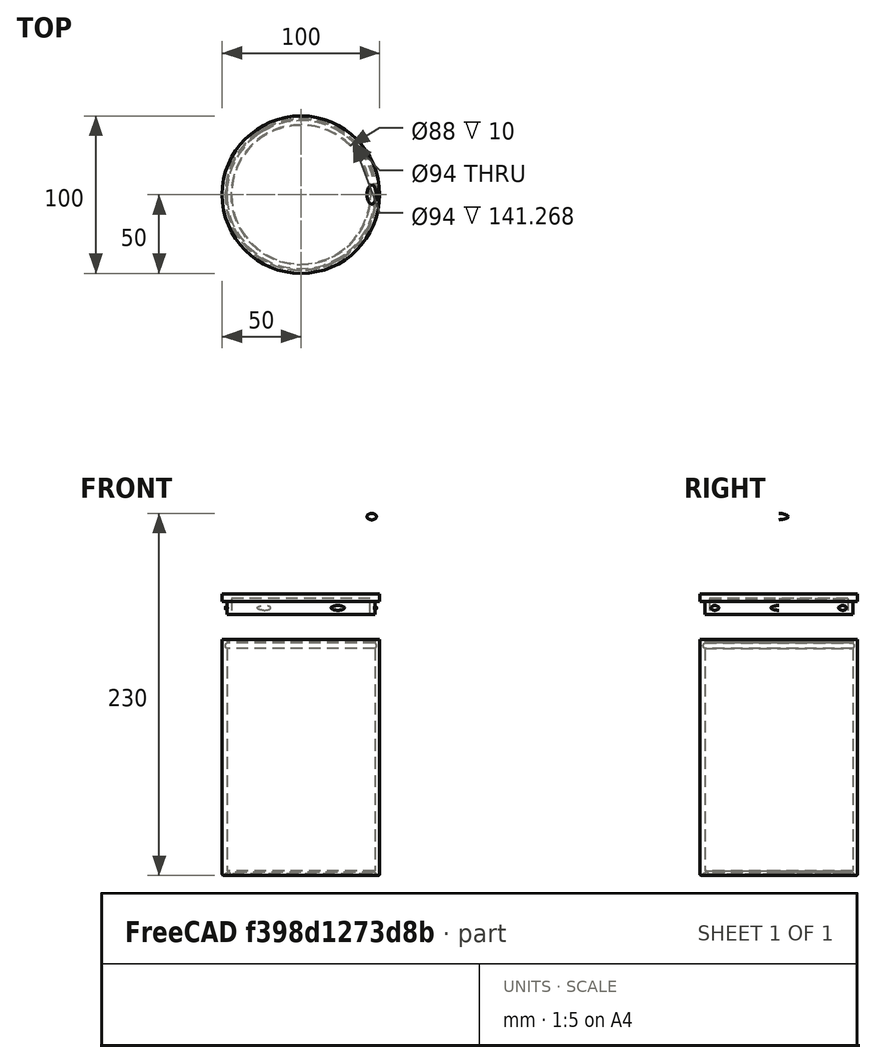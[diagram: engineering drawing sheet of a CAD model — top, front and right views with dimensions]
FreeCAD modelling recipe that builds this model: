
FCSTD DOCUMENT  (FreeCAD 0.20R28811 (Git))
Label: Cub_Escombreries
License: All rights reserved
LicenseURL: http://en.wikipedia.org/wiki/All_rights_reserved
objects: Part::Cylinder×7, Part::Cut×5, Part::Fuse×4, Part::Ellipsoid×2, Part::FeaturePython×2, Part::Torus×2, Part::Thickness×1, Part::Fillet×1, Part::Part2DObjectPython×1, Part::Chamfer×1
note: 24 computed .brp shape members not serialized (recipe doc carries the construction recipe); baked Part::Feature solids carry a one-line shape summary decoded from their .brp

FEATURE [Part::Cylinder] Cylinder
  Angle = 360
  AttacherType = Attacher::AttachEngine3D
  FirstAngle = 0
  Height = 150
  Radius = 50
  SecondAngle = 0
FEATURE [Part::Thickness] Thickness
  Faces = -> Cylinder [Face3]
  Intersection = false
  Join = 0
  Mode = 0
  SelfIntersection = false
  Value = -3
FEATURE [Part::Fillet] Fillet
  Base = -> Thickness
  Edges = 1 edges r=1: [Edge2]
FEATURE [Part::Cylinder] Cylinder001
  Angle = 360
  AttacherType = Attacher::AttachEngine3D
  FirstAngle = 0
  Height = 1
  Radius = 45
  SecondAngle = 0
FEATURE [Part::Cut] Cut  label="Cub"
  Base = -> Fillet
  Placement = pos=(0,0,-24) rot=(0,0,1;0rad)
  Refine = true
  Tool = -> Cylinder001
FEATURE [Part::Cylinder] Cylinder002
  Angle = 360
  AttacherType = Attacher::AttachEngine3D
  FirstAngle = 0
  Height = 5
  Placement = pos=(-7e-15,6e-15,208) rot=(0,0,1;0rad)
  Radius = 50
  SecondAngle = 0
FEATURE [Part::Cylinder] Cylinder003
  Angle = 360
  AttacherType = Attacher::AttachEngine3D
  FirstAngle = 0
  Height = 8
  Placement = pos=(-7.1e-15,5.1e-15,200) rot=(0,0,1;0rad)
  Radius = 47
  SecondAngle = 0
FEATURE [Part::Ellipsoid] Ellipsoid
  Angle1 = -90
  Angle2 = 90
  Angle3 = 360
  AttacherType = Attacher::AttachEngine3D
  Placement = pos=(45,7.1e-15,204) rot=(0,0,1;0rad)
  Radius1 = 2
  Radius2 = 3
  Radius3 = 6
FEATURE [Part::Fuse] Fusion  label="Tapa_sense_encaix"
  Base = -> Cylinder002
  Refine = true
  Tool = -> Cylinder003
FEATURE [Part::Part2DObjectPython] Circle  label="Circle_auxiliar_TBE"  # Draft 2D object (typed FeaturePython)
  Area = 0
  FirstAngle = 0
  LastAngle = 0
  MakeFace = false
  Placement = pos=(-7e-15,7e-15,204) rot=(1,0,0;3.14159rad)
  Radius = 50
FEATURE [Part::FeaturePython] Array  # Draft array (typed FeaturePython)
  AlwaysSyncPlacement = false
  Angle = 360
  ArrayType = 1
  Axis = (0,0,1)
  Base = -> Ellipsoid
  Center = (0,0,208)
  Count = 6
  ExpandArray = false
  Fuse = false
  IntervalAxis = (0,0,0)
  IntervalX = (50,0,0)
  IntervalY = (0,50,0)
  IntervalZ = (0,0,50)
  NumberCircles = 3
  NumberPolar = 6
  NumberX = 2
  NumberY = 2
  NumberZ = 1
  PlacementList = 6 placements: [(45,7.1e-15,204),(22.5,38.9711,204),(-22.5,38.9711,204),(-45,-1.58909e-15,204),(-22.5,-38.9711,204),(22.5,-38.9711,204)]
  RadialDistance = 50
  ScaleList = (6) [(1,1,1),(1,1,1),(1,1,1),(1,1,1),(1,1,1),(1,1,1)]
  Symmetry = 1
  TangentialDistance = 25
FEATURE [Part::Fuse] Fusion002  label="Tapa_amb_encaix"
  Base = -> Fusion
  Placement = pos=(0,0,-58) rot=(0,0,1;0rad)
  Refine = true
  Tool = -> Array
FEATURE [Part::Torus] Torus
  Angle1 = -180
  Angle2 = 180
  Angle3 = 360
  AttacherType = Attacher::AttachEngine3D
  Placement = pos=(0,0,-24) rot=(0,0,1;0rad)
  Radius1 = 46.2
  Radius2 = 2
FEATURE [Part::Cut] Cut001
  Base = -> Cut
  Refine = true
  Tool = -> Torus
FEATURE [Part::Cylinder] Cylinder004
  Angle = 360
  AttacherType = Attacher::AttachEngine3D
  FirstAngle = 0
  Height = 5
  Placement = pos=(-7e-15,6e-15,208) rot=(0,0,1;0rad)
  Radius = 50
  SecondAngle = 0
FEATURE [Part::Cylinder] Cylinder005
  Angle = 360
  AttacherType = Attacher::AttachEngine3D
  FirstAngle = 0
  Height = 8
  Placement = pos=(-7.1e-15,5.1e-15,200) rot=(0,0,1;0rad)
  Radius = 47
  SecondAngle = 0
FEATURE [Part::Ellipsoid] Ellipsoid001
  Angle1 = -90
  Angle2 = 90
  Angle3 = 360
  AttacherType = Attacher::AttachEngine3D
  Placement = pos=(45,7.1e-15,204) rot=(0,0,1;0rad)
  Radius1 = 2
  Radius2 = 3
  Radius3 = 6
FEATURE [Part::FeaturePython] Array001  # Draft array (typed FeaturePython)
  AlwaysSyncPlacement = false
  Angle = 360
  ArrayType = 1
  Axis = (0,0,1)
  Base = -> Ellipsoid001
  Center = (0,0,208)
  Count = 6
  ExpandArray = false
  Fuse = false
  IntervalAxis = (0,0,0)
  IntervalX = (50,0,0)
  IntervalY = (0,50,0)
  IntervalZ = (0,0,50)
  NumberCircles = 3
  NumberPolar = 6
  NumberX = 2
  NumberY = 2
  NumberZ = 1
  PlacementList = 6 placements: [(45,7.1e-15,204),(22.5,38.9711,204),(-22.5,38.9711,204),(-45,-1.58909e-15,204),(-22.5,-38.9711,204),(22.5,-38.9711,204)]
  RadialDistance = 50
  ScaleList = (6) [(1,1,1),(1,1,1),(1,1,1),(1,1,1),(1,1,1),(1,1,1)]
  Symmetry = 1
  TangentialDistance = 25
FEATURE [Part::Fuse] Fusion003  label="Tapa_sense_encaix001"
  Base = -> Cylinder004
  Refine = true
  Tool = -> Cylinder005
FEATURE [Part::Fuse] Fusion004  label="Tapa_amb_encaix001"
  Base = -> Fusion003
  Placement = pos=(0,0,-82) rot=(0,0,1;0rad)
  Refine = true
  Tool = -> Array001
FEATURE [Part::Cut] Cut002
  Base = -> Cut001
  Refine = true
  Tool = -> Fusion004
FEATURE [Part::Torus] Torus001
  Angle1 = -180
  Angle2 = 180
  Angle3 = 360
  AttacherType = Attacher::AttachEngine3D
  Placement = pos=(0,0,122) rot=(0,0,1;0rad)
  Radius1 = 46
  Radius2 = 2
FEATURE [Part::Cut] Cut003
  Base = -> Cut002
  Refine = true
  Tool = -> Torus001
FEATURE [Part::Chamfer] Chamfer  label="Cubell"
  Base = -> Cut003
  Edges = 1 edges r=1: [Edge8]
FEATURE [Part::Cylinder] Cylinder006
  Angle = 360
  AttacherType = Attacher::AttachEngine3D
  FirstAngle = 0
  Height = 10
  Placement = pos=(0,0,142) rot=(0,0,1;0rad)
  Radius = 44
  SecondAngle = 0
FEATURE [Part::Cut] Cut004  label="Tapa_amb_encaix002"
  Base = -> Fusion002
  Refine = true
  Tool = -> Cylinder006
